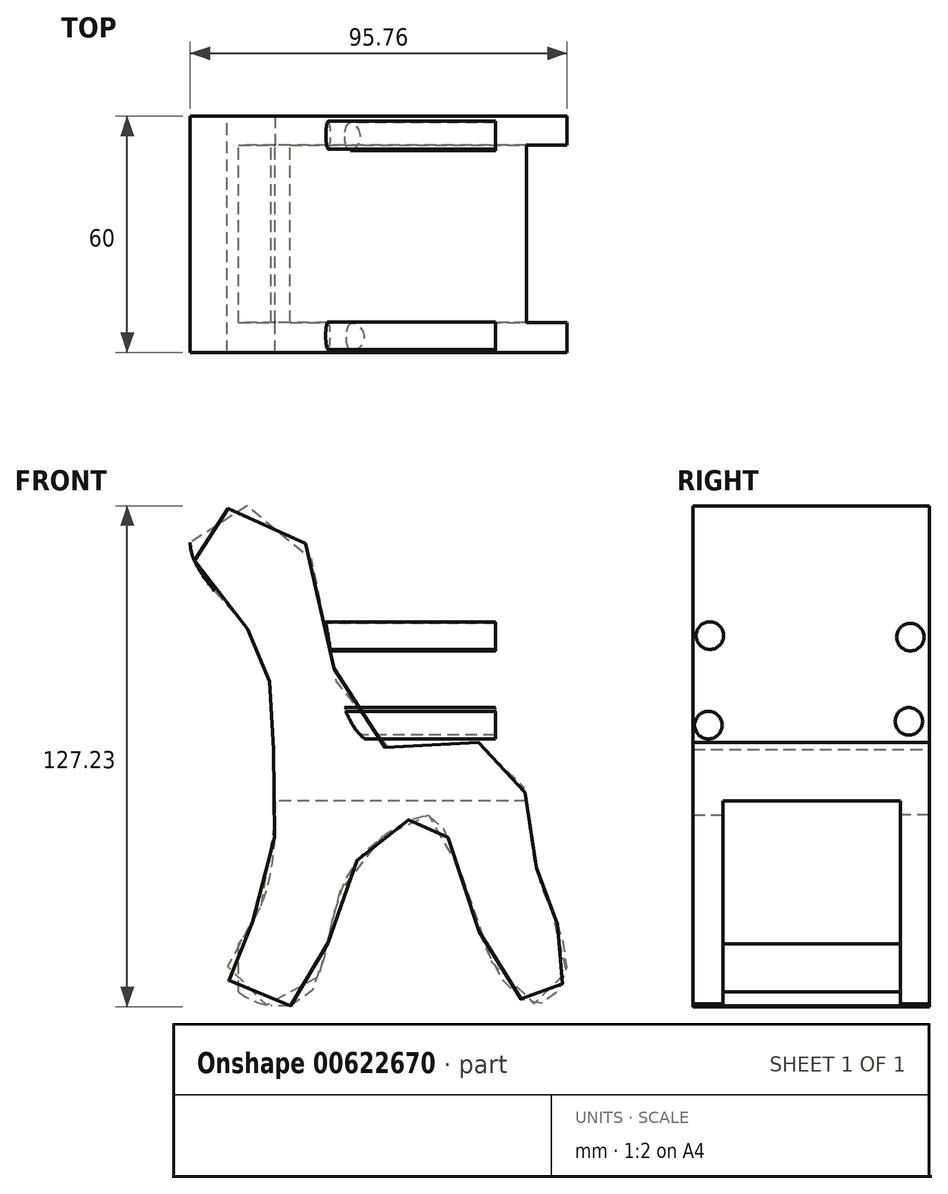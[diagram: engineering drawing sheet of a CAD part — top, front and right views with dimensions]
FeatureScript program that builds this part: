
annotation { "Feature Type Name" : "Feature", "Feature Type Description" : "" }
export const myFeature = defineFeature(function(context is Context, id is Id, definition is map)
    precondition{}
    {
        {
            var Q0;
            Q0=qCreatedBy(makeId("Front.planeOp"),FACE);
            var sketch = newSketch(context, id + "F0", { "sketchPlane" : qUnion([Q0])});
            skFitSpline(sketch, "E0", {"points": [v(-47.77, 36.24) * mm, v(-42.15, 22.63) * mm, v(-40.97, 0) * mm, v(-44.81, -35.05) * mm, v(-52.5, -53.1) * mm, v(-34.46, -58.72) * mm, v(-23.81, -29.43) * mm, v(-8.73, -13.46) * mm, v(0, -11.98) * mm, v(13.16, -46) * mm, v(25.88, -59.01) * mm, v(33.28, -51.02) * mm, v(28.84, -33.87) * mm, v(24.4, -17.9) * mm, v(15.83, 6.36) * mm, v(-18.2, 8.43) * mm, v(-37.42, 64.04) * mm, v(-61.97, 59.9) * mm, v(-47.77, 36.24) * mm]});
            skSolve(sketch);
        }
        {
            var Q0;
            Q0 = qSketchRegion(id + "F0", true);
            extrude(context, id + "F1", {"entities" : qUnion([Q0]), "depth" : 60 * mm, "offsetDistance" : 25.4 * mm});
        }
        {
            var Q0;
            Q0=qCreatedBy(makeId("Right.planeOp"),FACE);
            var sketch = newSketch(context, id + "F2", { "sketchPlane" : qUnion([Q0])});
            skLineSegment(sketch, "E1.bottom", {"start": v(-52.4, -59.57) * mm, "end": v(-7.35, -59.57) * mm});
            skLineSegment(sketch, "E1.top", {"start": v(-52.4, -7.57) * mm, "end": v(-7.35, -7.57) * mm});
            skLineSegment(sketch, "E1.left", {"start": v(-52.4, -59.57) * mm, "end": v(-52.4, -7.57) * mm});
            skLineSegment(sketch, "E1.right", {"start": v(-7.35, -59.57) * mm, "end": v(-7.35, -7.57) * mm});
            skSolve(sketch);
        }
        {
            var Q0;
            Q0 = qSketchRegion(id + "F2", true);
            extrude(context, id + "F3", {"entities" : qUnion([Q0]), "operationType" : NewBodyOperationType.REMOVE, "endBound" : BoundingType.THROUGH_ALL, "depth" : 25 * mm, "offsetDistance" : 25 * mm, "hasSecondDirection" : true, "secondDirectionOppositeDirection" : true, "secondDirectionDepth" : 50 * mm});
        }
        {
            var Q0;
            Q0=qCreatedBy(makeId("Right.planeOp"),FACE);
            cPlane(context, id + "F4", {"entities" : qUnion([Q0]), "cplaneType" : CPlaneType.OFFSET, "offset" : 30 * mm, "oppositeDirection" : true, "width" : 150 * mm, "height" : 150 * mm});
        }
        {
            var Q0;
            Q0=qCreatedBy(id+"F4.planeOp",FACE);
            var sketch = newSketch(context, id + "F5", { "sketchPlane" : qUnion([Q0])});
            skCircle(sketch, "E2", {"center": v(-55.73, 34.49) * mm, "radius": 3.5 * mm});
            skCircle(sketch, "E3", {"center": v(-56.1, 11.75) * mm, "radius": 3.5 * mm});
            skCircle(sketch, "E4", {"center": v(-4.8, 34.11) * mm, "radius": 3.5 * mm});
            skCircle(sketch, "E5", {"center": v(-5.17, 12.69) * mm, "radius": 3.5 * mm});
            skSolve(sketch);
        }
        {
            var Q0;
            Q0 = qSketchRegion(id + "F5", true);
            extrude(context, id + "F6", {"entities" : qUnion([Q0]), "operationType" : NewBodyOperationType.ADD, "depth" : 45.2 * mm, "offsetDistance" : 25 * mm});
        }
    });
